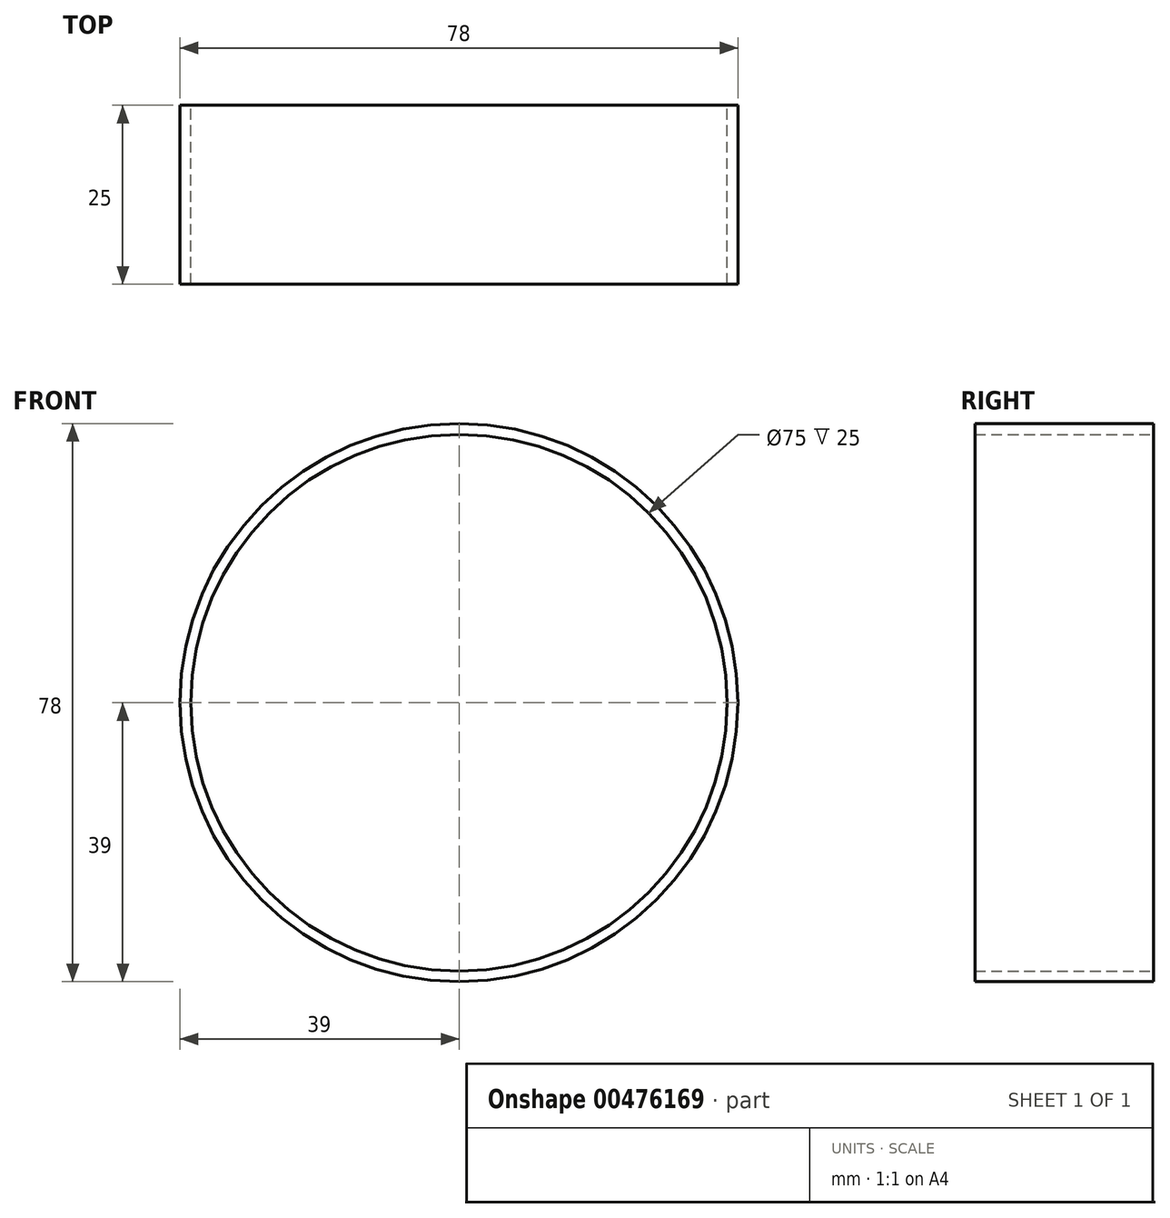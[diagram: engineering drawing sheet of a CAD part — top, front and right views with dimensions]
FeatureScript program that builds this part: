
annotation { "Feature Type Name" : "Feature", "Feature Type Description" : "" }
export const myFeature = defineFeature(function(context is Context, id is Id, definition is map)
    precondition{}
    {
        {
            var Q0;
            Q0=qCreatedBy(makeId("Front.planeOp"),FACE);
            var sketch = newSketch(context, id + "F0", { "sketchPlane" : qUnion([Q0])});
            skCircle(sketch, "E0", {"center": v(0, 0) * mm, "radius": 39 * mm});
            skCircle(sketch, "E1", {"center": v(0, 0) * mm, "radius": 37.5 * mm});
            skSolve(sketch);
        }
        {
            var Q0;
            Q0=makeQuery(id+"F0.imprint","IMPRINT",FACE,{"disambiguationData":[TD([[makeQuery(id+"F0.imprint","IMPRINT",EDGE,{"derivedFrom":sQuery(id+"F0.wireOp",EDGE,"E0")}),1.0]])]});
            extrude(context, id + "F1", {"entities" : qUnion([Q0]), "depth" : 25 * mm});
        }
    });
